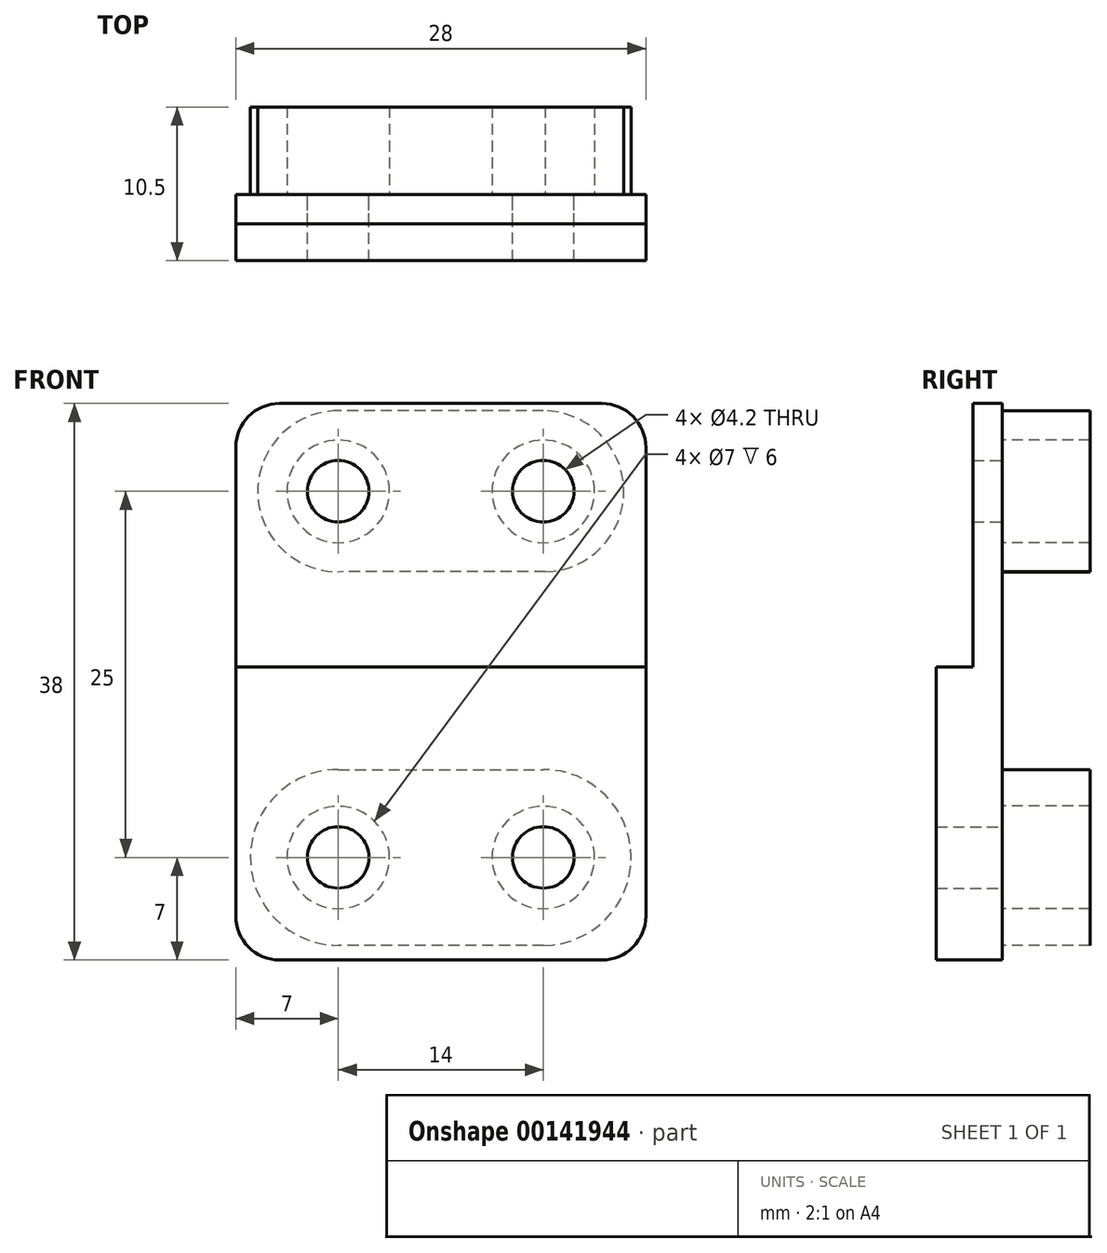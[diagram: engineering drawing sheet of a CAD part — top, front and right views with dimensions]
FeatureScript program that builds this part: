
annotation { "Feature Type Name" : "Feature", "Feature Type Description" : "" }
export const myFeature = defineFeature(function(context is Context, id is Id, definition is map)
    precondition{}
    {
        {
            var Q0;
            Q0=qCreatedBy(makeId("Front.planeOp"),FACE);
            var sketch = newSketch(context, id + "F0", { "sketchPlane" : qUnion([Q0])});
            skCircle(sketch, "E0", {"center": v(0, 0) * mm, "radius": 2.1 * mm});
            skCircle(sketch, "E1", {"center": v(0, -25) * mm, "radius": 2.1 * mm});
            skCircle(sketch, "E2", {"center": v(14, 0) * mm, "radius": 2.1 * mm});
            skCircle(sketch, "E3", {"center": v(14, -25) * mm, "radius": 2.1 * mm});
            skLineSegment(sketch, "E4.bottom", {"start": v(-7, 6) * mm, "end": v(21, 6) * mm});
            skLineSegment(sketch, "E4.top", {"start": v(-7, -32) * mm, "end": v(21, -32) * mm});
            skLineSegment(sketch, "E4.left", {"start": v(-7, 6) * mm, "end": v(-7, -32) * mm});
            skLineSegment(sketch, "E4.right", {"start": v(21, 6) * mm, "end": v(21, -32) * mm});
            skLineSegment(sketch, "E5", {"start": v(-7, -12) * mm, "end": v(21, -12) * mm});
            skSolve(sketch);
        }
        {
            var Q0;
            Q0=makeQuery(id+"F0.imprint","IMPRINT",FACE,{"disambiguationData":[TD([[makeQuery(id+"F0.imprint","IMPRINT",EDGE,{"derivedFrom":sQuery(id+"F0.wireOp",EDGE,"E0")}),-1.0]])]});
            extrude(context, id + "F1", {"entities" : qUnion([Q0]), "depth" : 2 * mm, "offsetDistance" : 25 * mm});
        }
        {
            var Q0;
            Q0=makeQuery(id+"F0.imprint","IMPRINT",FACE,{"disambiguationData":[TD([[makeQuery(id+"F0.imprint","IMPRINT",EDGE,{"derivedFrom":sQuery(id+"F0.wireOp",EDGE,"E1")}),-1.0]])]});
            extrude(context, id + "F2", {"entities" : qUnion([Q0]), "operationType" : NewBodyOperationType.ADD, "depth" : 4.5 * mm, "offsetDistance" : 25 * mm});
        }
        {
            var Q0;
            Q0=makeQuery(id+"F0.imprint","IMPRINT",FACE,{"disambiguationData":[TD([[makeQuery(id+"F0.imprint","IMPRINT",EDGE,{"derivedFrom":sQuery(id+"F0.wireOp",EDGE,"E0")}),-1.0]])]});
            var sketch = newSketch(context, id + "F3", { "sketchPlane" : qUnion([Q0])});
            skCircle(sketch, "E6", {"center": v(0, 0) * mm, "radius": 3.5 * mm});
            skCircle(sketch, "E7", {"center": v(14, 0) * mm, "radius": 3.5 * mm});
            skCircle(sketch, "E8", {"center": v(0, -25) * mm, "radius": 3.5 * mm});
            skCircle(sketch, "E9", {"center": v(14, -25) * mm, "radius": 3.5 * mm});
            skCircle(sketch, "E10", {"center": v(14, 0) * mm, "radius": 5.5 * mm});
            skCircle(sketch, "E11", {"center": v(0, 0) * mm, "radius": 5.5 * mm});
            skCircle(sketch, "E12", {"center": v(0, -25) * mm, "radius": 6 * mm});
            skCircle(sketch, "E13", {"center": v(14, -25) * mm, "radius": 6 * mm});
            skLineSegment(sketch, "E14", {"start": v(14.01, 5.5) * mm, "end": v(0, 5.5) * mm});
            skLineSegment(sketch, "E15", {"start": v(14.13, -5.5) * mm, "end": v(0, -5.5) * mm});
            skLineSegment(sketch, "E16", {"start": v(0, -19) * mm, "end": v(14, -19) * mm});
            skLineSegment(sketch, "E17", {"start": v(14.03, -31) * mm, "end": v(0, -31) * mm});
            skSolve(sketch);
        }
        {
            var Q0;
            {var subQ0=sQuery(id+"F3.wireOp",EDGE,"E14");Q0=makeQuery(id+"F3.imprint","IMPRINT",FACE,{"disambiguationData":[TD([[makeQuery(id+"F3.imprint","IMPRINT",EDGE,{"derivedFrom":subQ0}),1.0]])]});}
            var Q1;
            Q1=makeQuery(id+"F3.imprint","IMPRINT",FACE,{"disambiguationData":[TD([[makeQuery(id+"F3.imprint","IMPRINT",EDGE,{"derivedFrom":sQuery(id+"F3.wireOp",EDGE,"E6")}),-1.0]])]});
            var Q2;
            Q2=makeQuery(id+"F3.imprint","IMPRINT",FACE,{"disambiguationData":[TD([[makeQuery(id+"F3.imprint","IMPRINT",EDGE,{"derivedFrom":sQuery(id+"F3.wireOp",EDGE,"E7")}),-1.0]])]});
            var Q3;
            {var subQ0=sQuery(id+"F3.wireOp",EDGE,"E16");Q3=makeQuery(id+"F3.imprint","IMPRINT",FACE,{"disambiguationData":[TD([[makeQuery(id+"F3.imprint","IMPRINT",EDGE,{"derivedFrom":subQ0}),-1.0]])]});}
            var Q4;
            Q4=makeQuery(id+"F3.imprint","IMPRINT",FACE,{"disambiguationData":[TD([[makeQuery(id+"F3.imprint","IMPRINT",EDGE,{"derivedFrom":sQuery(id+"F3.wireOp",EDGE,"E8")}),-1.0]])]});
            var Q5;
            Q5=makeQuery(id+"F3.imprint","IMPRINT",FACE,{"disambiguationData":[TD([[makeQuery(id+"F3.imprint","IMPRINT",EDGE,{"derivedFrom":sQuery(id+"F3.wireOp",EDGE,"E9")}),-1.0]])]});
            extrude(context, id + "F4", {"entities" : qUnion([Q0, Q1, Q2, Q3, Q4, Q5]), "operationType" : NewBodyOperationType.ADD, "oppositeDirection" : true, "depth" : 6 * mm, "offsetDistance" : 25 * mm});
        }
        {
            var Q0;
            Q0=makeQuery(id+"F2.opExtrude","SWEPT_EDGE",EDGE,{"disambiguationData":[OSD([sQuery(id+"F0.wireOp",EDGE,"E4.top"),sQuery(id+"F0.wireOp",EDGE,"E4.right")])]});
            var Q1;
            Q1=makeQuery(id+"F1.opExtrude","SWEPT_EDGE",EDGE,{"disambiguationData":[OSD([sQuery(id+"F0.wireOp",EDGE,"E4.bottom"),sQuery(id+"F0.wireOp",EDGE,"E4.right")])]});
            var Q2;
            Q2=makeQuery(id+"F1.opExtrude","SWEPT_EDGE",EDGE,{"disambiguationData":[OSD([sQuery(id+"F0.wireOp",EDGE,"E4.bottom"),sQuery(id+"F0.wireOp",EDGE,"E4.left")])]});
            var Q3;
            Q3=makeQuery(id+"F2.opExtrude","SWEPT_EDGE",EDGE,{"disambiguationData":[OSD([sQuery(id+"F0.wireOp",EDGE,"E4.top"),sQuery(id+"F0.wireOp",EDGE,"E4.left")])]});
            fillet(context, id + "F5", {"entities" : qUnion([Q0, Q1, Q2, Q3]), "radius" : 3 * mm, "tangentPropagation" : true, "allowEdgeOverflow" : false});
        }
    });
